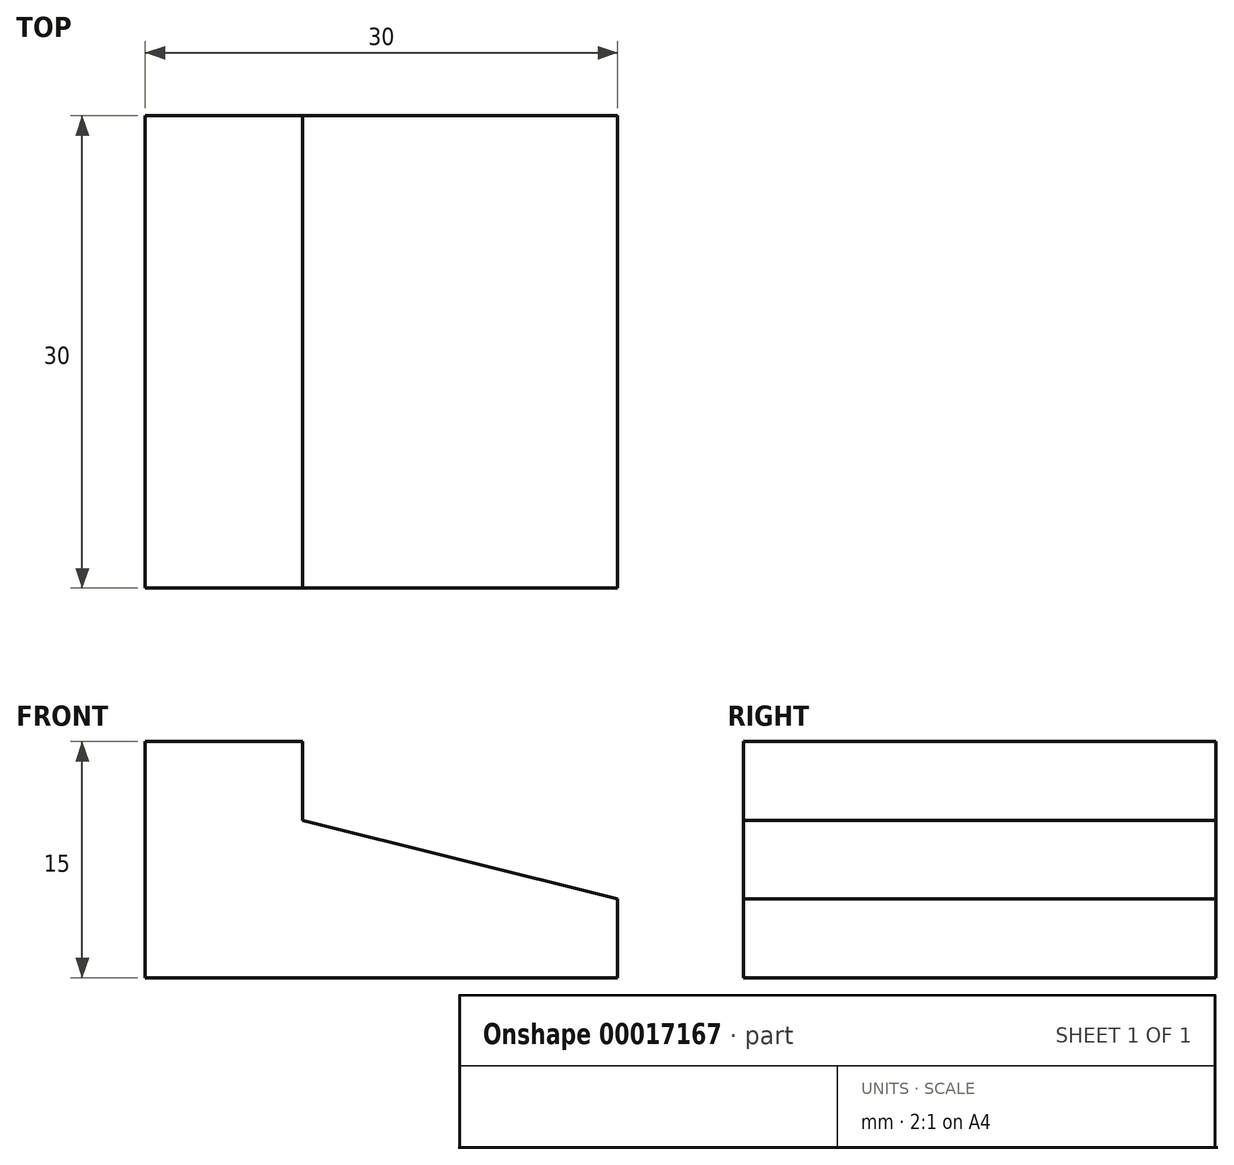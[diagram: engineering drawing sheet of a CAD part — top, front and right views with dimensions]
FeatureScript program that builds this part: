
annotation { "Feature Type Name" : "Feature", "Feature Type Description" : "" }
export const myFeature = defineFeature(function(context is Context, id is Id, definition is map)
    precondition{}
    {
        {
            var Q0;
            Q0=qCreatedBy(makeId("Front.planeOp"),FACE);
            var sketch = newSketch(context, id + "F0", { "sketchPlane" : qUnion([Q0])});
            skLineSegment(sketch, "E0.bottom", {"start": v(-44.36, 28.34) * mm, "end": v(-34.36, 28.34) * mm});
            skLineSegment(sketch, "E0.top", {"start": v(-44.36, 13.34) * mm, "end": v(-14.36, 13.34) * mm});
            skLineSegment(sketch, "E0.left", {"start": v(-44.36, 28.34) * mm, "end": v(-44.36, 13.34) * mm});
            skLineSegment(sketch, "E0.right", {"start": v(-14.36, 18.34) * mm, "end": v(-14.36, 13.34) * mm});
            skPoint(sketch, "E1.orphan", {"position": v(-34.36, 13.34) * mm});
            skPoint(sketch, "E2.end.orphan", {"position": v(-34.36, 20.84) * mm});
            skLineSegment(sketch, "E3", {"start": v(-34.36, 28.34) * mm, "end": v(-34.36, 23.34) * mm});
            skLineSegment(sketch, "E4", {"start": v(-34.36, 23.34) * mm, "end": v(-14.36, 18.34) * mm});
            skSolve(sketch);
        }
        {
            var Q0;
            Q0 = qSketchRegion(id + "F0", true);
            extrude(context, id + "F1", {"entities" : qUnion([Q0]), "depth" : 30 * mm});
        }
    });
